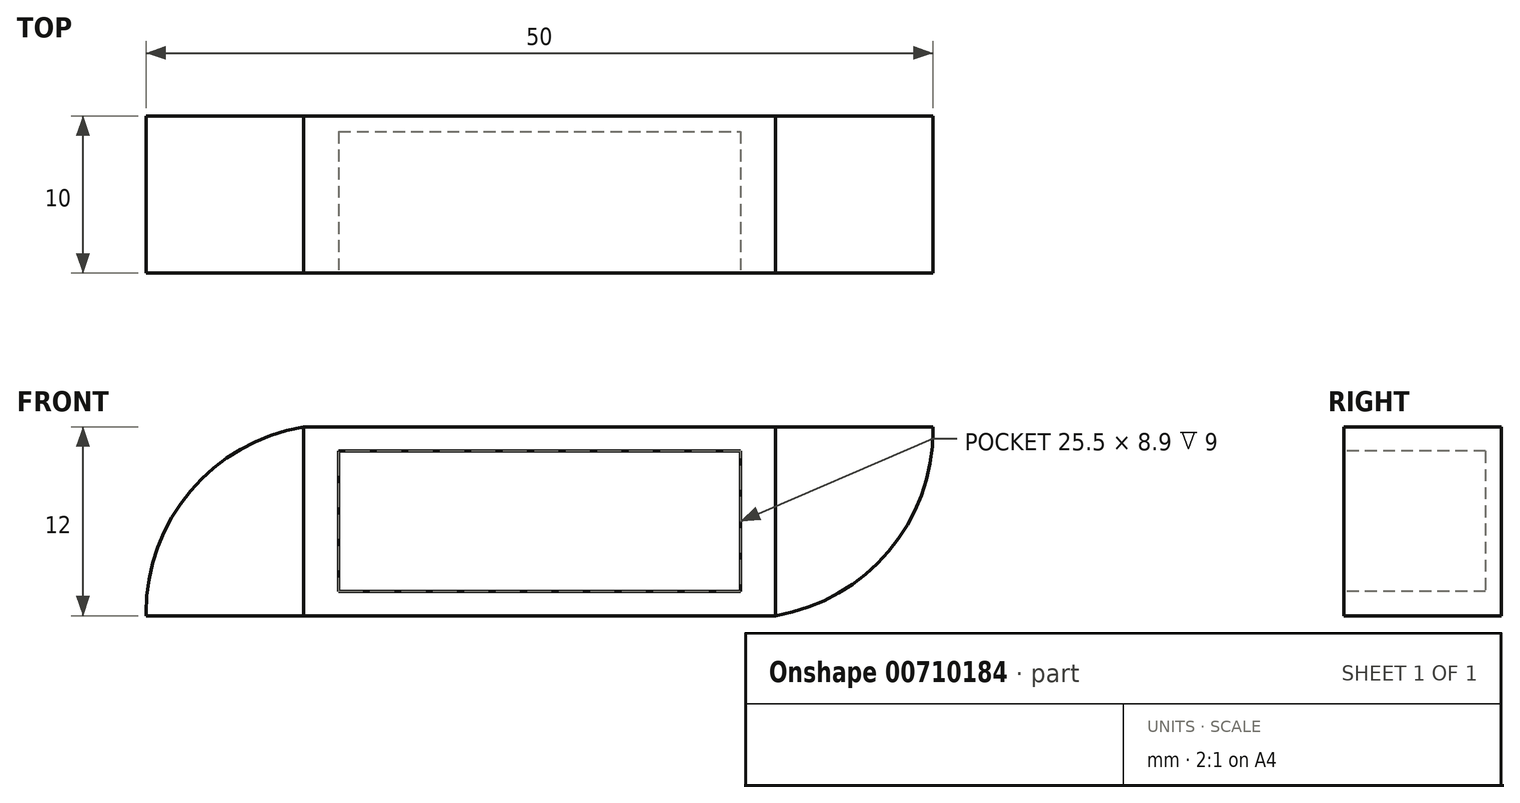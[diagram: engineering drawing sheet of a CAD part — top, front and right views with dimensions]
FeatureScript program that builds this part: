
annotation { "Feature Type Name" : "Feature", "Feature Type Description" : "" }
export const myFeature = defineFeature(function(context is Context, id is Id, definition is map)
    precondition{}
    {
        {
            var Q0;
            Q0=qCreatedBy(makeId("Top.planeOp"),FACE);
            var sketch = newSketch(context, id + "F0", { "sketchPlane" : qUnion([Q0])});
            skLineSegment(sketch, "E0", {"start": v(0, 0) * mm, "end": v(25.5, 0) * mm});
            skLineSegment(sketch, "E1", {"start": v(25.5, 0) * mm, "end": v(25.5, 8.9) * mm});
            skLineSegment(sketch, "E2", {"start": v(25.5, 8.9) * mm, "end": v(0, 8.9) * mm});
            skLineSegment(sketch, "E3", {"start": v(0, 8.9) * mm, "end": v(0, 0) * mm});
            skSolve(sketch);
        }
        {
            var Q0;
            Q0=makeQuery(id+"F0.imprint","IMPRINT",FACE,{"disambiguationData":[TD([[makeQuery(id+"F0.imprint","IMPRINT",EDGE,{"derivedFrom":sQuery(id+"F0.wireOp",EDGE,"E0")}),1.0]])]});
            extrude(context, id + "F1", {"entities" : qUnion([Q0]), "depth" : 8.9 * mm, "offsetDistance" : 25 * mm});
        }
        {
            var Q0;
            Q0=makeQuery(id+"F1.opExtrude","SWEPT_FACE",FACE,{"disambiguationData":[OSD([sQuery(id+"F0.wireOp",EDGE,"E0")])]});
            var sketch = newSketch(context, id + "F2", { "sketchPlane" : qUnion([Q0])});
            skLineSegment(sketch, "E4.bottom", {"start": v(-2.25, 10.45) * mm, "end": v(27.75, 10.45) * mm});
            skLineSegment(sketch, "E4.top", {"start": v(-2.25, -1.55) * mm, "end": v(27.75, -1.55) * mm});
            skLineSegment(sketch, "E4.left", {"start": v(-2.25, 10.45) * mm, "end": v(-2.25, -1.55) * mm});
            skLineSegment(sketch, "E4.right", {"start": v(27.75, 10.45) * mm, "end": v(27.75, -1.55) * mm});
            skPoint(sketch, "E4.middle", {"position": v(12.75, 4.45) * mm});
            skSolve(sketch);
        }
        {
            var Q0;
            {var subQ0=sQuery(id+"F0.wireOp",EDGE,"E0");Q0=makeQuery(id+"F2.imprint","IMPRINT",FACE,{"disambiguationData":[TD([[makeQuery(id+"F2.imprint","IMPRINT",EDGE,{"derivedFrom":makeQuery(id+"F1.opExtrude","CAP_EDGE",EDGE,{"disambiguationData":[OSD([subQ0])],"isStart":true})}),1.0]])]});}
            var Q1;
            Q1=makeQuery(id+"F2.imprint","IMPRINT",FACE,{"disambiguationData":[TD([[makeQuery(id+"F2.imprint","IMPRINT",EDGE,{"derivedFrom":sQuery(id+"F2.wireOp",EDGE,"E4.bottom")}),-1.0]])]});
            extrude(context, id + "F3", {"entities" : qUnion([Q0, Q1]), "oppositeDirection" : true, "depth" : 10 * mm, "offsetDistance" : 25 * mm});
        }
        {
            var Q0;
            Q0=makeQuery(id+"F1.opExtrude","SWEPT_FACE",FACE,{"disambiguationData":[OSD([sQuery(id+"F0.wireOp",EDGE,"E0")])]});
            extrude(context, id + "F4", {"entities" : qUnion([Q0]), "operationType" : NewBodyOperationType.REMOVE, "oppositeDirection" : true, "depth" : 9 * mm, "offsetDistance" : 25 * mm});
        }
        {
            var Q0;
            Q0=makeQuery(id+"F3.opExtrude","SWEPT_FACE",FACE,{"disambiguationData":[OSD([sQuery(id+"F2.wireOp",EDGE,"E4.left")])]});
            extrude(context, id + "F5", {"entities" : qUnion([Q0]), "depth" : 10 * mm, "offsetDistance" : 25 * mm});
        }
        {
            var Q0;
            Q0=makeQuery(id+"F3.opExtrude","SWEPT_FACE",FACE,{"disambiguationData":[OSD([sQuery(id+"F2.wireOp",EDGE,"E4.right")])]});
            extrude(context, id + "F6", {"entities" : qUnion([Q0]), "depth" : 10 * mm, "offsetDistance" : 25 * mm});
        }
        {
            var Q0;
            Q0=makeQuery(id+"F3.opExtrude","SWEPT_FACE",FACE,{"disambiguationData":[OSD([sQuery(id+"F2.wireOp",EDGE,"E4.bottom")])]});
            var sketch = newSketch(context, id + "F7", { "sketchPlane" : qUnion([Q0])});
            skLineSegment(sketch, "E5", {"start": v(12.75, 0) * mm, "end": v(18.75, 0) * mm});
            skLineSegment(sketch, "E6", {"start": v(18.75, 0) * mm, "end": v(18.75, 10) * mm});
            skLineSegment(sketch, "E7", {"start": v(18.75, 10) * mm, "end": v(12.75, 10) * mm});
            skLineSegment(sketch, "E8", {"start": v(12.75, 10) * mm, "end": v(6.75, 10) * mm});
            skLineSegment(sketch, "E9", {"start": v(6.75, 10) * mm, "end": v(6.75, 0) * mm});
            skLineSegment(sketch, "E10", {"start": v(12.75, 0) * mm, "end": v(6.75, 0) * mm});
            skSolve(sketch);
        }
        {
            var Q0;
            Q0=makeQuery(id+"F3.opExtrude","SWEPT_FACE",FACE,{"disambiguationData":[OSD([sQuery(id+"F2.wireOp",EDGE,"E4.top")])]});
            var sketch = newSketch(context, id + "F8", { "sketchPlane" : qUnion([Q0])});
            skLineSegment(sketch, "E11", {"start": v(12.75, -10) * mm, "end": v(18.75, -10) * mm});
            skLineSegment(sketch, "E12", {"start": v(18.75, -10) * mm, "end": v(18.75, 0) * mm});
            skLineSegment(sketch, "E13", {"start": v(12.75, 0) * mm, "end": v(18.75, 0) * mm});
            skLineSegment(sketch, "E14", {"start": v(12.75, 0) * mm, "end": v(6.75, 0) * mm});
            skLineSegment(sketch, "E15", {"start": v(6.75, 0) * mm, "end": v(6.75, -10) * mm});
            skLineSegment(sketch, "E16", {"start": v(6.75, -10) * mm, "end": v(12.75, -10) * mm});
            skSolve(sketch);
        }
        {
            var Q0;
            Q0=makeQuery(id+"FosGmJq5SILQGFZ_5.opExtrude","CAP_EDGE",EDGE,{"disambiguationData":[OSD([sQuery(id+"F8.wireOp",EDGE,"E15")])],"isStart":false});
            var Q1;
            Q1=makeQuery(id+"F5.opExtrude","CAP_EDGE",EDGE,{"disambiguationData":[OSD([sQuery(id+"F2.wireOp",EDGE,"E4.bottom"),sQuery(id+"F2.wireOp",EDGE,"E4.left")])],"isStart":false});
            var Q2;
            Q2=makeQuery(id+"FqWK5za6CKHgtiD_4.opExtrude","CAP_EDGE",EDGE,{"disambiguationData":[OSD([sQuery(id+"F7.wireOp",EDGE,"E6")])],"isStart":false});
            var Q3;
            Q3=makeQuery(id+"F6.opExtrude","CAP_EDGE",EDGE,{"disambiguationData":[OSD([sQuery(id+"F2.wireOp",EDGE,"E4.top"),sQuery(id+"F2.wireOp",EDGE,"E4.right")])],"isStart":false});
            fillet(context, id + "F9", {"entities" : qUnion([Q0, Q1, Q2, Q3]), "radius" : 12 * mm, "tangentPropagation" : true, "allowEdgeOverflow" : false});
        }
    });
